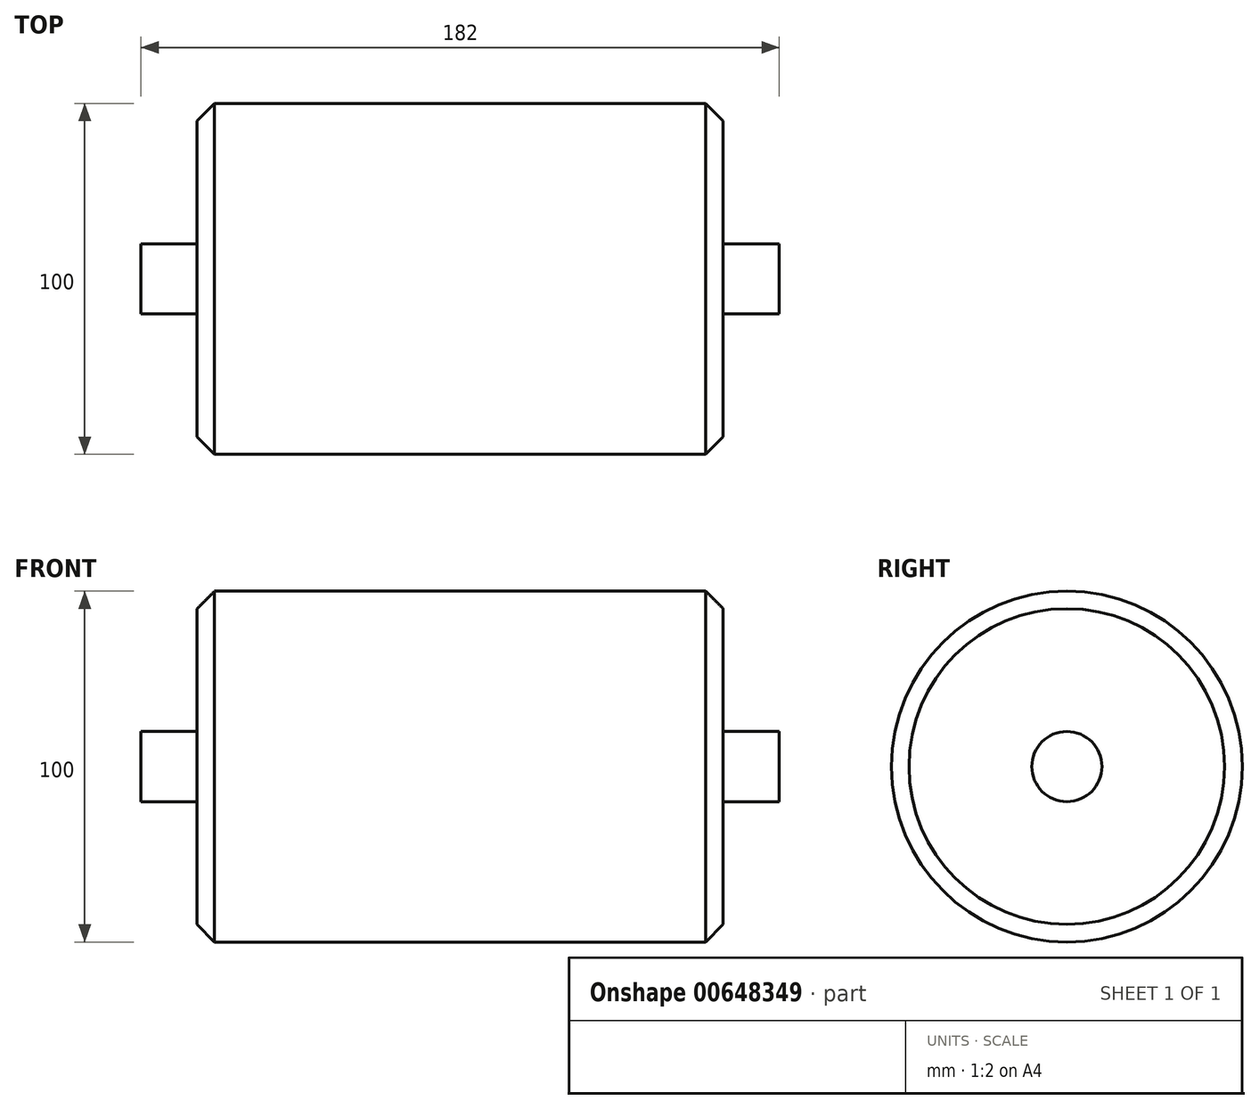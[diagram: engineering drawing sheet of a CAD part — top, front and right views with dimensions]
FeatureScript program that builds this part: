
annotation { "Feature Type Name" : "Feature", "Feature Type Description" : "" }
export const myFeature = defineFeature(function(context is Context, id is Id, definition is map)
    precondition{}
    {
        {
            var Q0;
            Q0=qCreatedBy(makeId("Front.planeOp"),FACE);
            var sketch = newSketch(context, id + "F0", { "sketchPlane" : qUnion([Q0])});
            skLineSegment(sketch, "E0.bottom", {"start": v(0, 0) * mm, "end": v(150, 0) * mm});
            skLineSegment(sketch, "E0.top", {"start": v(0, 50) * mm, "end": v(150, 50) * mm});
            skLineSegment(sketch, "E0.left", {"start": v(0, 0) * mm, "end": v(0, 50) * mm});
            skLineSegment(sketch, "E0.right", {"start": v(150, 0) * mm, "end": v(150, 50) * mm});
            skLineSegment(sketch, "E1.bottom", {"start": v(0, 0) * mm, "end": v(-16, 0) * mm});
            skLineSegment(sketch, "E1.top", {"start": v(0, 10) * mm, "end": v(-16, 10) * mm});
            skLineSegment(sketch, "E1.left", {"start": v(0, 0) * mm, "end": v(0, 10) * mm});
            skLineSegment(sketch, "E1.right", {"start": v(-16, 0) * mm, "end": v(-16, 10) * mm});
            skLineSegment(sketch, "E2.bottom", {"start": v(150, 0) * mm, "end": v(166, 0) * mm});
            skLineSegment(sketch, "E2.top", {"start": v(150, 10) * mm, "end": v(166, 10) * mm});
            skLineSegment(sketch, "E2.left", {"start": v(150, 0) * mm, "end": v(150, 10) * mm});
            skLineSegment(sketch, "E2.right", {"start": v(166, 0) * mm, "end": v(166, 10) * mm});
            skSolve(sketch);
        }
        {
            var Q0;
            Q0=makeQuery(id+"F0.imprint","IMPRINT",FACE,{"disambiguationData":[TD([[makeQuery(id+"F0.imprint","IMPRINT",EDGE,{"derivedFrom":sQuery(id+"F0.wireOp",EDGE,"E0.bottom")}),1.0]])]});
            var Q1;
            Q1=makeQuery(id+"F0.imprint","IMPRINT",FACE,{"disambiguationData":[TD([[makeQuery(id+"F0.imprint","IMPRINT",EDGE,{"derivedFrom":sQuery(id+"F0.wireOp",EDGE,"E1.bottom")}),-1.0]])]});
            var Q2;
            Q2=makeQuery(id+"F0.imprint","IMPRINT",FACE,{"disambiguationData":[TD([[makeQuery(id+"F0.imprint","IMPRINT",EDGE,{"derivedFrom":sQuery(id+"F0.wireOp",EDGE,"E2.bottom")}),1.0]])]});
            var Q3;
            Q3=sQuery(id+"F0.wireOp",EDGE,"E0.bottom");
            revolve(context, id + "F1", {"entities" : qUnion([Q0, Q1, Q2]), "axis" : qUnion([Q3]), "revolveType" : RevolveType.FULL});
        }
        {
            var Q0;
            Q0=makeQuery(id+"F1.opRevolve","SWEPT_EDGE",EDGE,{"disambiguationData":[OSD([sQuery(id+"F0.wireOp",EDGE,"E0.top"),sQuery(id+"F0.wireOp",EDGE,"E0.right")])]});
            var Q1;
            Q1=makeQuery(id+"F1.opRevolve","SWEPT_EDGE",EDGE,{"disambiguationData":[OSD([sQuery(id+"F0.wireOp",EDGE,"E0.top"),sQuery(id+"F0.wireOp",EDGE,"E0.left")])]});
            chamfer(context, id + "F2", {"entities" : qUnion([Q0, Q1]), "chamferType" : ChamferType.OFFSET_ANGLE, "width" : 5 * mm, "oppositeDirection" : false, "angle" : 45 * degree, "tangentPropagation" : true});
        }
    });
